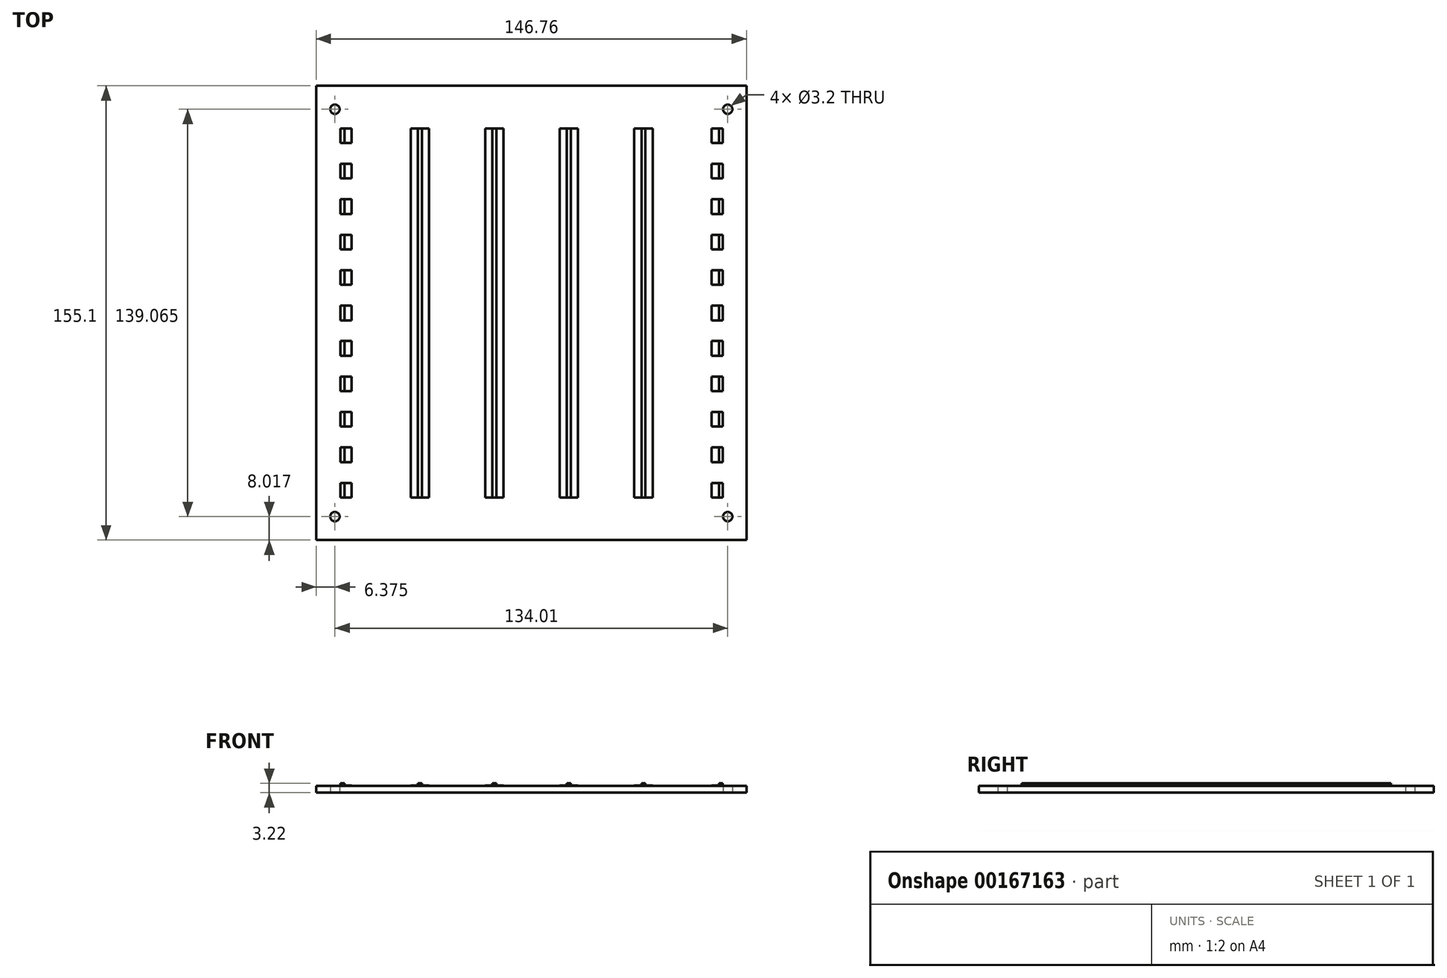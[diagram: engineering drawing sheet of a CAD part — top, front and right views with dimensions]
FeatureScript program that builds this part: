
annotation { "Feature Type Name" : "Feature", "Feature Type Description" : "" }
export const myFeature = defineFeature(function(context is Context, id is Id, definition is map)
    precondition{}
    {
        {
            var Q0;
            Q0=qCreatedBy(makeId("Top.planeOp"),FACE);
            var sketch = newSketch(context, id + "F0", { "sketchPlane" : qUnion([Q0])});
            skLineSegment(sketch, "E0.bottom", {"start": v(-73.38, 77.55) * mm, "end": v(73.38, 77.55) * mm});
            skLineSegment(sketch, "E0.top", {"start": v(-73.38, -77.55) * mm, "end": v(73.38, -77.55) * mm});
            skLineSegment(sketch, "E0.left", {"start": v(-73.38, 77.55) * mm, "end": v(-73.38, -77.55) * mm});
            skLineSegment(sketch, "E0.right", {"start": v(73.38, 77.55) * mm, "end": v(73.38, -77.55) * mm});
            skPoint(sketch, "E0.middle", {"position": v(0, 0) * mm});
            skCircle(sketch, "E1", {"center": v(-67, 69.53) * mm, "radius": 1.6 * mm});
            skCircle(sketch, "E2", {"center": v(67, 69.53) * mm, "radius": 1.6 * mm});
            skCircle(sketch, "E3", {"center": v(67, -69.53) * mm, "radius": 1.6 * mm});
            skCircle(sketch, "E4", {"center": v(-67, -69.53) * mm, "radius": 1.6 * mm});
            skSolve(sketch);
        }
        {
            var Q0;
            Q0 = qSketchRegion(id + "F0", true);
            extrude(context, id + "F1", {"entities" : qUnion([Q0]), "depth" : 2.37 * mm});
        }
        {
            var Q0;
            Q0=makeQuery(id+"F1.opExtrude","CAP_FACE",FACE,{"disambiguationData":[OSD([sQuery(id+"F0.wireOp",EDGE,"E0.bottom"),sQuery(id+"F0.wireOp",EDGE,"E0.top"),sQuery(id+"F0.wireOp",EDGE,"E0.left"),sQuery(id+"F0.wireOp",EDGE,"E0.right"),sQuery(id+"F0.wireOp",EDGE,"E1"),sQuery(id+"F0.wireOp",EDGE,"E2"),sQuery(id+"F0.wireOp",EDGE,"E3"),sQuery(id+"F0.wireOp",EDGE,"E4")])],"isStart":false});
            var sketch = newSketch(context, id + "F2", { "sketchPlane" : qUnion([Q0])});
            skLineSegment(sketch, "E5.bottom", {"start": v(64.03, 63) * mm, "end": v(65.32, 63) * mm});
            skLineSegment(sketch, "E5.top", {"start": v(64.03, -63) * mm, "end": v(65.32, -63) * mm});
            skLineSegment(sketch, "E5.left", {"start": v(64.03, 63) * mm, "end": v(64.03, -63) * mm});
            skLineSegment(sketch, "E5.right", {"start": v(65.33, 63) * mm, "end": v(65.33, -63) * mm});
            skLineSegment(sketch, "E6.bottom", {"start": v(37.62, 63) * mm, "end": v(38.93, 63) * mm});
            skLineSegment(sketch, "E6.top", {"start": v(37.63, -63) * mm, "end": v(38.93, -63) * mm});
            skLineSegment(sketch, "E6.left", {"start": v(37.63, 63) * mm, "end": v(37.63, -63) * mm});
            skLineSegment(sketch, "E6.right", {"start": v(38.93, 63) * mm, "end": v(38.93, -63) * mm});
            skLineSegment(sketch, "E7.bottom", {"start": v(12.12, 63) * mm, "end": v(13.42, 63) * mm});
            skLineSegment(sketch, "E7.top", {"start": v(12.13, -63) * mm, "end": v(13.43, -63) * mm});
            skLineSegment(sketch, "E7.left", {"start": v(12.13, 63) * mm, "end": v(12.13, -63) * mm});
            skLineSegment(sketch, "E7.right", {"start": v(13.43, 63) * mm, "end": v(13.43, -63) * mm});
            skLineSegment(sketch, "E8.bottom", {"start": v(-38.68, 63) * mm, "end": v(-37.38, 63) * mm});
            skLineSegment(sketch, "E8.top", {"start": v(-38.67, -63) * mm, "end": v(-37.37, -63) * mm});
            skLineSegment(sketch, "E8.left", {"start": v(-38.67, 63) * mm, "end": v(-38.67, -63) * mm});
            skLineSegment(sketch, "E8.right", {"start": v(-37.37, 63) * mm, "end": v(-37.37, -63) * mm});
            skLineSegment(sketch, "E9.bottom", {"start": v(-13.28, 63) * mm, "end": v(-11.98, 63) * mm});
            skLineSegment(sketch, "E9.top", {"start": v(-13.28, -63) * mm, "end": v(-11.98, -63) * mm});
            skLineSegment(sketch, "E9.left", {"start": v(-13.27, 63) * mm, "end": v(-13.27, -63) * mm});
            skLineSegment(sketch, "E9.right", {"start": v(-11.97, 63) * mm, "end": v(-11.97, -63) * mm});
            skLineSegment(sketch, "E10.bottom", {"start": v(-65.08, 63) * mm, "end": v(-63.78, 63) * mm});
            skLineSegment(sketch, "E10.top", {"start": v(-65.08, -63) * mm, "end": v(-63.78, -63) * mm});
            skLineSegment(sketch, "E10.left", {"start": v(-65.07, 63) * mm, "end": v(-65.07, -63) * mm});
            skLineSegment(sketch, "E10.right", {"start": v(-63.77, 63) * mm, "end": v(-63.77, -63) * mm});
            skLineSegment(sketch, "E11", {"start": v(-73.38, -63) * mm, "end": v(73.38, -63) * mm, "construction": true});
            skSolve(sketch);
        }
        {
            var Q0;
            Q0 = qSketchRegion(id + "F2", true);
            extrude(context, id + "F3", {"entities" : qUnion([Q0]), "operationType" : NewBodyOperationType.ADD, "depth" : .85 * mm});
        }
        {
            var Q0;
            Q0=makeQuery(id+"F1.opExtrude","CAP_FACE",FACE,{"disambiguationData":[OSD([sQuery(id+"F0.wireOp",EDGE,"E0.bottom"),sQuery(id+"F0.wireOp",EDGE,"E0.top"),sQuery(id+"F0.wireOp",EDGE,"E0.left"),sQuery(id+"F0.wireOp",EDGE,"E0.right"),sQuery(id+"F0.wireOp",EDGE,"E1"),sQuery(id+"F0.wireOp",EDGE,"E2"),sQuery(id+"F0.wireOp",EDGE,"E3"),sQuery(id+"F0.wireOp",EDGE,"E4")])],"isStart":false});
            var sketch = newSketch(context, id + "F4", { "sketchPlane" : qUnion([Q0])});
            skLineSegment(sketch, "E12.bottom", {"start": v(-63.78, 63) * mm, "end": v(-61.28, 63) * mm});
            skLineSegment(sketch, "E12.top", {"start": v(-63.77, -63) * mm, "end": v(-61.28, -63) * mm});
            skLineSegment(sketch, "E12.left", {"start": v(-63.78, 63) * mm, "end": v(-63.78, -63) * mm});
            skLineSegment(sketch, "E12.right", {"start": v(-61.28, 63) * mm, "end": v(-61.28, -63) * mm});
            skLineSegment(sketch, "E13.bottom", {"start": v(-38.68, 63) * mm, "end": v(-41.17, 63) * mm});
            skLineSegment(sketch, "E13.top", {"start": v(-38.67, -63) * mm, "end": v(-41.17, -63) * mm});
            skLineSegment(sketch, "E13.left", {"start": v(-38.68, 63) * mm, "end": v(-38.67, -63) * mm});
            skLineSegment(sketch, "E13.right", {"start": v(-41.17, 63) * mm, "end": v(-41.17, -63) * mm});
            skLineSegment(sketch, "E14.bottom", {"start": v(-37.37, -63) * mm, "end": v(-34.87, -63) * mm});
            skLineSegment(sketch, "E14.top", {"start": v(-37.38, 63) * mm, "end": v(-34.87, 63) * mm});
            skLineSegment(sketch, "E14.left", {"start": v(-37.37, -63) * mm, "end": v(-37.38, 63) * mm});
            skLineSegment(sketch, "E14.right", {"start": v(-34.87, -63) * mm, "end": v(-34.87, 63) * mm});
            skLineSegment(sketch, "E15.bottom", {"start": v(-13.28, 63) * mm, "end": v(-15.78, 63) * mm});
            skLineSegment(sketch, "E15.top", {"start": v(-13.27, -63) * mm, "end": v(-15.77, -63) * mm});
            skLineSegment(sketch, "E15.left", {"start": v(-13.28, 63) * mm, "end": v(-13.27, -63) * mm});
            skLineSegment(sketch, "E15.right", {"start": v(-15.78, 63) * mm, "end": v(-15.77, -63) * mm});
            skLineSegment(sketch, "E16.bottom", {"start": v(-11.97, -63) * mm, "end": v(-9.47, -63) * mm});
            skLineSegment(sketch, "E16.top", {"start": v(-11.98, 63) * mm, "end": v(-9.48, 63) * mm});
            skLineSegment(sketch, "E16.left", {"start": v(-11.97, -63) * mm, "end": v(-11.98, 63) * mm});
            skLineSegment(sketch, "E16.right", {"start": v(-9.47, -63) * mm, "end": v(-9.48, 63) * mm});
            skLineSegment(sketch, "E17.bottom", {"start": v(12.12, 63) * mm, "end": v(9.63, 63) * mm});
            skLineSegment(sketch, "E17.top", {"start": v(12.13, -63) * mm, "end": v(9.63, -63) * mm});
            skLineSegment(sketch, "E17.left", {"start": v(12.12, 63) * mm, "end": v(12.13, -63) * mm});
            skLineSegment(sketch, "E17.right", {"start": v(9.63, 63) * mm, "end": v(9.63, -63) * mm});
            skLineSegment(sketch, "E18.bottom", {"start": v(13.43, -63) * mm, "end": v(15.93, -63) * mm});
            skLineSegment(sketch, "E18.top", {"start": v(13.42, 63) * mm, "end": v(15.93, 63) * mm});
            skLineSegment(sketch, "E18.left", {"start": v(13.43, -63) * mm, "end": v(13.42, 63) * mm});
            skLineSegment(sketch, "E18.right", {"start": v(15.93, -63) * mm, "end": v(15.93, 63) * mm});
            skLineSegment(sketch, "E19.bottom", {"start": v(37.62, 63) * mm, "end": v(35.12, 63) * mm});
            skLineSegment(sketch, "E19.top", {"start": v(37.63, -63) * mm, "end": v(35.13, -63) * mm});
            skLineSegment(sketch, "E19.left", {"start": v(37.62, 63) * mm, "end": v(37.63, -63) * mm});
            skLineSegment(sketch, "E19.right", {"start": v(35.12, 63) * mm, "end": v(35.13, -63) * mm});
            skLineSegment(sketch, "E20.bottom", {"start": v(38.93, -63) * mm, "end": v(41.43, -63) * mm});
            skLineSegment(sketch, "E20.top", {"start": v(38.92, 63) * mm, "end": v(41.43, 63) * mm});
            skLineSegment(sketch, "E20.left", {"start": v(38.93, -63) * mm, "end": v(38.92, 63) * mm});
            skLineSegment(sketch, "E20.right", {"start": v(41.43, -63) * mm, "end": v(41.43, 63) * mm});
            skLineSegment(sketch, "E21.bottom", {"start": v(64.03, -63) * mm, "end": v(61.53, -63) * mm});
            skLineSegment(sketch, "E21.top", {"start": v(64.03, 63) * mm, "end": v(61.52, 63) * mm});
            skLineSegment(sketch, "E21.left", {"start": v(64.03, -63) * mm, "end": v(64.03, 63) * mm});
            skLineSegment(sketch, "E21.right", {"start": v(61.53, -63) * mm, "end": v(61.52, 63) * mm});
            skPoint(sketch, "E22.top.end.orphan", {"position": v(68.08, -63) * mm});
            skSolve(sketch);
        }
        {
            var Q0;
            Q0 = qSketchRegion(id + "F4", true);
            extrude(context, id + "F5", {"entities" : qUnion([Q0]), "operationType" : NewBodyOperationType.ADD, "depth" : .1 * mm});
        }
        {
            var Q0;
            Q0=makeQuery(id+"F3.opExtrude","CAP_FACE",FACE,{"disambiguationData":[OSD([sQuery(id+"F2.wireOp",EDGE,"E10.bottom"),sQuery(id+"F2.wireOp",EDGE,"E10.top"),sQuery(id+"F2.wireOp",EDGE,"E10.left"),sQuery(id+"F2.wireOp",EDGE,"E10.right")])],"isStart":false});
            var sketch = newSketch(context, id + "F6", { "sketchPlane" : qUnion([Q0])});
            skLineSegment(sketch, "E23.bottom", {"start": v(-66.38, -58) * mm, "end": v(-58.37, -58) * mm});
            skLineSegment(sketch, "E23.top", {"start": v(-66.38, -50.9) * mm, "end": v(-58.37, -50.9) * mm});
            skLineSegment(sketch, "E23.left", {"start": v(-66.38, -58) * mm, "end": v(-66.38, -50.9) * mm});
            skLineSegment(sketch, "E23.right", {"start": v(-58.37, -58) * mm, "end": v(-58.37, -50.9) * mm});
            skLineSegment(sketch, "E24.bottom", {"start": v(-66.38, -45.9) * mm, "end": v(-58.38, -45.9) * mm});
            skLineSegment(sketch, "E24.top", {"start": v(-66.38, -38.8) * mm, "end": v(-58.38, -38.8) * mm});
            skLineSegment(sketch, "E24.left", {"start": v(-66.37, -45.9) * mm, "end": v(-66.37, -38.8) * mm});
            skLineSegment(sketch, "E24.right", {"start": v(-58.37, -45.9) * mm, "end": v(-58.37, -38.8) * mm});
            skLineSegment(sketch, "E25.bottom", {"start": v(-66.38, -33.8) * mm, "end": v(-58.38, -33.8) * mm});
            skLineSegment(sketch, "E25.top", {"start": v(-66.38, -26.7) * mm, "end": v(-58.38, -26.7) * mm});
            skLineSegment(sketch, "E25.left", {"start": v(-66.37, -33.8) * mm, "end": v(-66.37, -26.7) * mm});
            skLineSegment(sketch, "E25.right", {"start": v(-58.37, -33.8) * mm, "end": v(-58.37, -26.7) * mm});
            skLineSegment(sketch, "E26", {"start": v(-66.37, 58) * mm, "end": v(-66.38, -80.85) * mm, "construction": true});
            skLineSegment(sketch, "E27.bottom", {"start": v(-66.38, -21.7) * mm, "end": v(-58.37, -21.7) * mm});
            skLineSegment(sketch, "E27.top", {"start": v(-66.38, -14.6) * mm, "end": v(-58.37, -14.6) * mm});
            skLineSegment(sketch, "E27.left", {"start": v(-66.37, -21.7) * mm, "end": v(-66.37, -14.6) * mm});
            skLineSegment(sketch, "E27.right", {"start": v(-58.37, -21.7) * mm, "end": v(-58.37, -14.6) * mm});
            skLineSegment(sketch, "E28.bottom", {"start": v(-66.38, -9.6) * mm, "end": v(-58.37, -9.6) * mm});
            skLineSegment(sketch, "E28.top", {"start": v(-66.38, -2.5) * mm, "end": v(-58.37, -2.5) * mm});
            skLineSegment(sketch, "E28.left", {"start": v(-66.37, -9.6) * mm, "end": v(-66.37, -2.5) * mm});
            skLineSegment(sketch, "E28.right", {"start": v(-58.37, -9.6) * mm, "end": v(-58.37, -2.5) * mm});
            skLineSegment(sketch, "E29.bottom", {"start": v(-66.38, 2.5) * mm, "end": v(-58.38, 2.5) * mm});
            skLineSegment(sketch, "E29.top", {"start": v(-66.38, 9.6) * mm, "end": v(-58.38, 9.6) * mm});
            skLineSegment(sketch, "E29.left", {"start": v(-66.37, 2.5) * mm, "end": v(-66.37, 9.6) * mm});
            skLineSegment(sketch, "E29.right", {"start": v(-58.37, 2.5) * mm, "end": v(-58.37, 9.6) * mm});
            skLineSegment(sketch, "E30.bottom", {"start": v(-66.37, 14.6) * mm, "end": v(-58.37, 14.6) * mm});
            skLineSegment(sketch, "E30.top", {"start": v(-66.37, 21.7) * mm, "end": v(-58.37, 21.7) * mm});
            skLineSegment(sketch, "E30.left", {"start": v(-66.37, 14.6) * mm, "end": v(-66.37, 21.7) * mm});
            skLineSegment(sketch, "E30.right", {"start": v(-58.38, 14.6) * mm, "end": v(-58.38, 21.7) * mm});
            skLineSegment(sketch, "E31.bottom", {"start": v(-66.37, 26.7) * mm, "end": v(-58.37, 26.7) * mm});
            skLineSegment(sketch, "E31.top", {"start": v(-66.37, 33.8) * mm, "end": v(-58.37, 33.8) * mm});
            skLineSegment(sketch, "E31.left", {"start": v(-66.37, 26.7) * mm, "end": v(-66.37, 33.8) * mm});
            skLineSegment(sketch, "E31.right", {"start": v(-58.38, 26.7) * mm, "end": v(-58.38, 33.8) * mm});
            skLineSegment(sketch, "E32.bottom", {"start": v(-66.37, 38.8) * mm, "end": v(-58.37, 38.8) * mm});
            skLineSegment(sketch, "E32.top", {"start": v(-66.37, 45.9) * mm, "end": v(-58.37, 45.9) * mm});
            skLineSegment(sketch, "E32.left", {"start": v(-66.37, 38.8) * mm, "end": v(-66.37, 45.9) * mm});
            skLineSegment(sketch, "E32.right", {"start": v(-58.38, 38.8) * mm, "end": v(-58.38, 45.9) * mm});
            skLineSegment(sketch, "E33.bottom", {"start": v(-66.38, 50.9) * mm, "end": v(-58.38, 50.9) * mm});
            skLineSegment(sketch, "E33.top", {"start": v(-66.38, 58) * mm, "end": v(-58.38, 58) * mm});
            skLineSegment(sketch, "E33.left", {"start": v(-66.38, 50.9) * mm, "end": v(-66.38, 58) * mm});
            skLineSegment(sketch, "E33.right", {"start": v(-58.37, 50.9) * mm, "end": v(-58.37, 58) * mm});
            skLineSegment(sketch, "E34.trimOffspring", {"start": v(-66.37, 58) * mm, "end": v(-66.37, -12.03) * mm, "construction": true});
            skLineSegment(sketch, "E35.bottom", {"start": v(59.38, -58) * mm, "end": v(67.38, -58) * mm});
            skLineSegment(sketch, "E35.top", {"start": v(59.38, -50.9) * mm, "end": v(67.38, -50.9) * mm});
            skLineSegment(sketch, "E35.left", {"start": v(59.37, -58) * mm, "end": v(59.37, -50.9) * mm});
            skLineSegment(sketch, "E35.right", {"start": v(67.37, -58) * mm, "end": v(67.37, -50.9) * mm});
            skLineSegment(sketch, "E36.bottom", {"start": v(59.38, -45.9) * mm, "end": v(67.38, -45.9) * mm});
            skLineSegment(sketch, "E36.top", {"start": v(59.38, -38.8) * mm, "end": v(67.38, -38.8) * mm});
            skLineSegment(sketch, "E36.left", {"start": v(59.37, -45.9) * mm, "end": v(59.37, -38.8) * mm});
            skLineSegment(sketch, "E36.right", {"start": v(67.37, -45.9) * mm, "end": v(67.37, -38.8) * mm});
            skLineSegment(sketch, "E37.bottom", {"start": v(59.38, -33.8) * mm, "end": v(67.38, -33.8) * mm});
            skLineSegment(sketch, "E37.top", {"start": v(59.38, -26.7) * mm, "end": v(67.38, -26.7) * mm});
            skLineSegment(sketch, "E37.left", {"start": v(59.37, -33.8) * mm, "end": v(59.37, -26.7) * mm});
            skLineSegment(sketch, "E37.right", {"start": v(67.37, -33.8) * mm, "end": v(67.37, -26.7) * mm});
            skLineSegment(sketch, "E38", {"start": v(59.38, 58) * mm, "end": v(59.37, -80.85) * mm, "construction": true});
            skLineSegment(sketch, "E39.bottom", {"start": v(59.38, -21.7) * mm, "end": v(67.38, -21.7) * mm});
            skLineSegment(sketch, "E39.top", {"start": v(59.38, -14.6) * mm, "end": v(67.38, -14.6) * mm});
            skLineSegment(sketch, "E39.left", {"start": v(59.38, -21.7) * mm, "end": v(59.38, -14.6) * mm});
            skLineSegment(sketch, "E39.right", {"start": v(67.38, -21.7) * mm, "end": v(67.38, -14.6) * mm});
            skLineSegment(sketch, "E40.bottom", {"start": v(59.38, -9.6) * mm, "end": v(67.38, -9.6) * mm});
            skLineSegment(sketch, "E40.top", {"start": v(59.38, -2.5) * mm, "end": v(67.38, -2.5) * mm});
            skLineSegment(sketch, "E40.left", {"start": v(59.38, -9.6) * mm, "end": v(59.38, -2.5) * mm});
            skLineSegment(sketch, "E40.right", {"start": v(67.38, -9.6) * mm, "end": v(67.38, -2.5) * mm});
            skLineSegment(sketch, "E41.bottom", {"start": v(59.38, 2.5) * mm, "end": v(67.38, 2.5) * mm});
            skLineSegment(sketch, "E41.top", {"start": v(59.38, 9.6) * mm, "end": v(67.38, 9.6) * mm});
            skLineSegment(sketch, "E41.left", {"start": v(59.38, 2.5) * mm, "end": v(59.38, 9.6) * mm});
            skLineSegment(sketch, "E41.right", {"start": v(67.37, 2.5) * mm, "end": v(67.37, 9.6) * mm});
            skLineSegment(sketch, "E42.bottom", {"start": v(59.38, 14.6) * mm, "end": v(67.38, 14.6) * mm});
            skLineSegment(sketch, "E42.top", {"start": v(59.38, 21.7) * mm, "end": v(67.38, 21.7) * mm});
            skLineSegment(sketch, "E42.left", {"start": v(59.38, 14.6) * mm, "end": v(59.38, 21.7) * mm});
            skLineSegment(sketch, "E42.right", {"start": v(67.38, 14.6) * mm, "end": v(67.38, 21.7) * mm});
            skLineSegment(sketch, "E43.bottom", {"start": v(59.38, 26.7) * mm, "end": v(67.38, 26.7) * mm});
            skLineSegment(sketch, "E43.top", {"start": v(59.38, 33.8) * mm, "end": v(67.38, 33.8) * mm});
            skLineSegment(sketch, "E43.left", {"start": v(59.38, 26.7) * mm, "end": v(59.38, 33.8) * mm});
            skLineSegment(sketch, "E43.right", {"start": v(67.38, 26.7) * mm, "end": v(67.38, 33.8) * mm});
            skLineSegment(sketch, "E44.bottom", {"start": v(59.38, 38.8) * mm, "end": v(67.38, 38.8) * mm});
            skLineSegment(sketch, "E44.top", {"start": v(59.38, 45.9) * mm, "end": v(67.38, 45.9) * mm});
            skLineSegment(sketch, "E44.left", {"start": v(59.38, 38.8) * mm, "end": v(59.38, 45.9) * mm});
            skLineSegment(sketch, "E44.right", {"start": v(67.38, 38.8) * mm, "end": v(67.38, 45.9) * mm});
            skLineSegment(sketch, "E45.bottom", {"start": v(59.38, 50.9) * mm, "end": v(67.38, 50.9) * mm});
            skLineSegment(sketch, "E45.top", {"start": v(59.38, 58) * mm, "end": v(67.38, 58) * mm});
            skLineSegment(sketch, "E45.left", {"start": v(59.38, 50.9) * mm, "end": v(59.38, 58) * mm});
            skLineSegment(sketch, "E45.right", {"start": v(67.38, 50.9) * mm, "end": v(67.38, 58) * mm});
            skLineSegment(sketch, "E46.trimOffspring", {"start": v(59.38, 58) * mm, "end": v(59.38, -1.44) * mm, "construction": true});
            skSolve(sketch);
        }
        {
            var Q0;
            Q0 = qSketchRegion(id + "F6", true);
            extrude(context, id + "F7", {"entities" : qUnion([Q0]), "operationType" : NewBodyOperationType.REMOVE, "oppositeDirection" : true, "depth" : .85 * mm});
        }
    });
